# Revit family: xHand_Dryer-Wall_Mounted-Bobrick-QuietDry-B-77X_Series
name_source: partatom
category: Specialty Equipment
revit_build: Autodesk Revit 2014 (Build: 20130308_1515(x64)
units: mm (PartAtom-declared; Revit-internal decimal feet)

## types (2) — shared parameters
115V AC, 12 Amp, 50/60 Hz, 1380 Watts, Single Phase, cULus Listed. = Yes
208-240V AC, 5.5-6.3 Amp, 50/60 Hz, 1380 Watts, Single Phase, cULus Listed and CE marked. = No
ADA Compliant = Yes
Assembly Code = E1010
Default Elevation = 48 "
Depth = 7.4 "
Description = QuietDry Series, DuraDry Surface-Mounted High Speed Hand Dryer
Frequency = 60 Hz
Height = 12.1 "
Installation Type = Surface Mounted
Manufacturer = Bobrick Washroom Equipment, Inc.
Phase = 1
Price = Prices may vary. Please consult Manufacturer Representative for most up-to-date price list.
Product Documentation Link = http://bobrick.com
Product Page URL = http://bobrick.com
Specification = Surface-mounted hand dryer shall have a one-piece, cast aluminum cover with either white high-gloss epoxy finish electrostatically applied (B-770) or chrome finish (B-778). Motor shall be 75W (1/10hp) universal type on resilient mountings with shielded ball-bearings, equipped with an integral automatic thermal-overload device. Unit is equipped with single outlet for efficient dry time. The unit shall be uniquely designed to have a sound pressure level of 72dB(A) measured at 39" (1 metre) from source. Heating element shall be located on the inlet side of the fan; shall heat without hot spots; shall be inaccessible to vandals; protected by an integral thermal-overload device. Dryer controller shall automatically energize the dryer when hands are detected in the infrared sensing zone. The dryer will either automatically turn off immediately after hands are removed, or after 1-1/2 minutes of continuous usage. The controller will automatically reset after any obstructions are removed. The unit shall be CE marked, cULus Listed, & VDE approved. Unit shall comply with EU Directive “Restriction of Hazardous Substances” (RoHS) requirements for non-use of certain hazardous substances in the production of electronic products. Unit shall be protected by a limited 10 year warranty on all parts except motor brushes, in turn warranted for 3 years from date of purchase.
Type Comments = Specify Voltage.
URL = http://bobrick.com
Voltage = 115 V
Warranty Information = 10-Year Limited Warranty
Wattage = 1380 W
Width = 10.5 "

## per-type parameters (varying)
| type | Finish | Material |
| B-770 | Aluminum-Bobrick-White-Glossy | Aluminum-Bobrick-White-Glossy |
| B-778 | Aluminum-Bobrick-Stainless Steel-Chrome | Aluminum-Bobrick-Stainless Steel-Chrome |

note: column(s) folded — value = type name in every type: Model

## geometry (parser evidence)
native form markers: Sweep x2
no freeform markers — native parametric forms only
